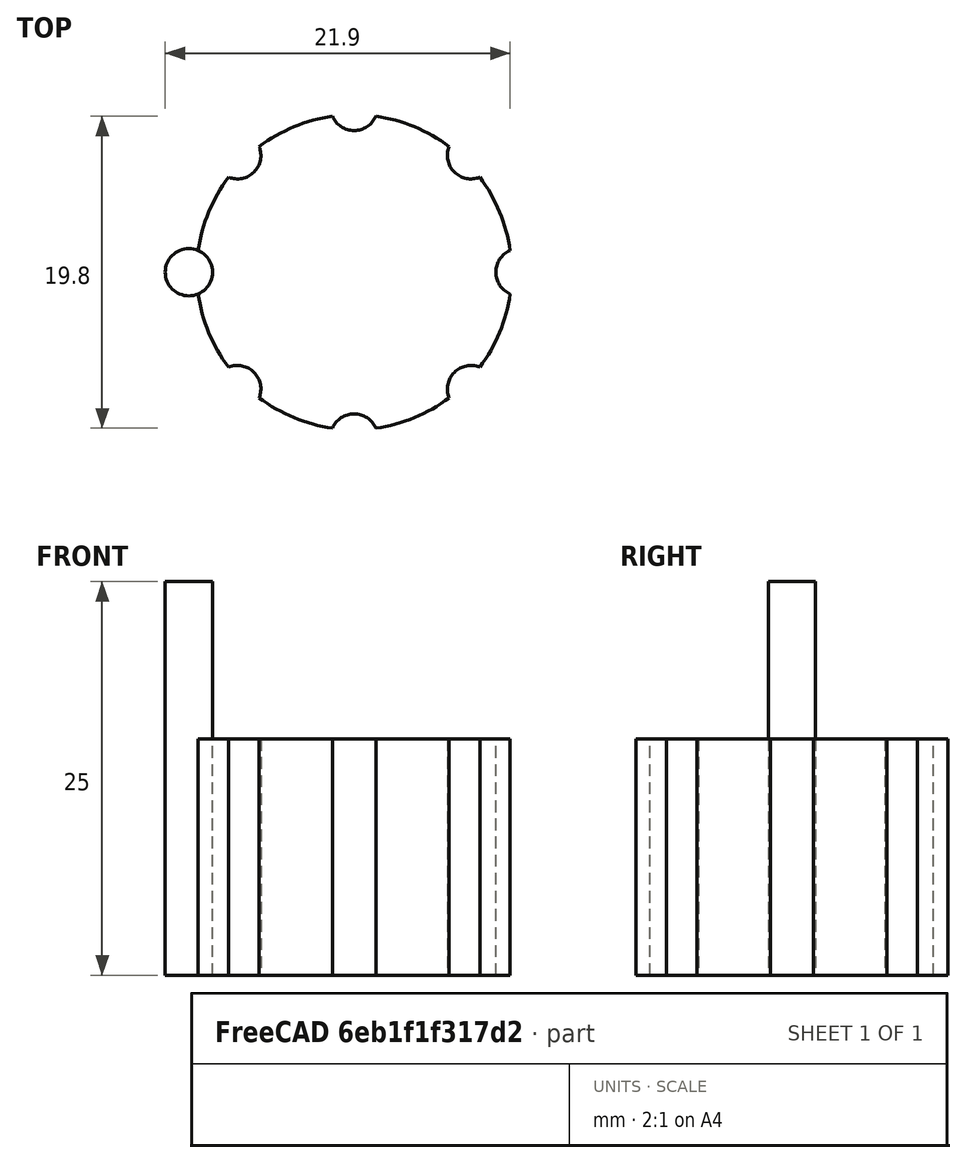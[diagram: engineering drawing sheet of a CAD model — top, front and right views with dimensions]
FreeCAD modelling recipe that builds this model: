
FCSTD DOCUMENT  (FreeCAD 0.21R33694 (Git))
Label: OJT1_T11R01_botoseleccio
License: All rights reserved
LicenseURL: https://en.wikipedia.org/wiki/All_rights_reserved
objects: Part::Cylinder×2, Part::FeaturePython×1, Part::Cut×1
note: 3 computed .brp shape members not serialized (recipe doc carries the construction recipe); baked Part::Feature solids carry a one-line shape summary decoded from their .brp

FEATURE [Part::Cylinder] Cylinder001  label="Cilindre001"
  Angle = 360
  AttacherType = Attacher::AttachEngine3D
  FirstAngle = 0
  Height = 25
  Radius = 1.5
  SecondAngle = 0
FEATURE [Part::Cylinder] Cylinder  label="Cilindre_gran"
  Angle = 360
  AttacherType = Attacher::AttachEngine3D
  FirstAngle = 0
  Height = 15
  Placement = pos=(10.5,0,0) rot=(0,0,1;0rad)
  Radius = 10
  SecondAngle = 0
FEATURE [Part::FeaturePython] Array  # Draft array (typed FeaturePython)
  AlwaysSyncPlacement = false
  Angle = 360
  ArrayType = 1
  Axis = (0,0,1)
  Base = -> Cylinder001
  Center = (10.5,0,0)
  Count = 8
  ExpandArray = false
  Fuse = false
  IntervalAxis = (0,0,0)
  IntervalX = (100,0,0)
  IntervalY = (0,100,0)
  IntervalZ = (0,0,100)
  NumberCircles = 3
  NumberPolar = 8
  NumberX = 2
  NumberY = 2
  NumberZ = 1
  PlacementList = 8 placements: [(0,0,0),(3.07538,-7.42462,0),(10.5,-10.5,0),(17.9246,-7.42462,0),(21,-1.28588e-15,0),(17.9246,7.42462,0),(10.5,10.5,0),(3.07538,7.42462,0)]
  RadialDistance = 50
  ScaleList = (8) [(1,1,1),(1,1,1),(1,1,1),(1,1,1),(1,1,1),(1,1,1),(1,1,1),(1,1,1)]
  Symmetry = 1
  TangentialDistance = 25
FEATURE [Part::Cut] Cut
  Base = -> Cylinder
  Tool = -> Array
